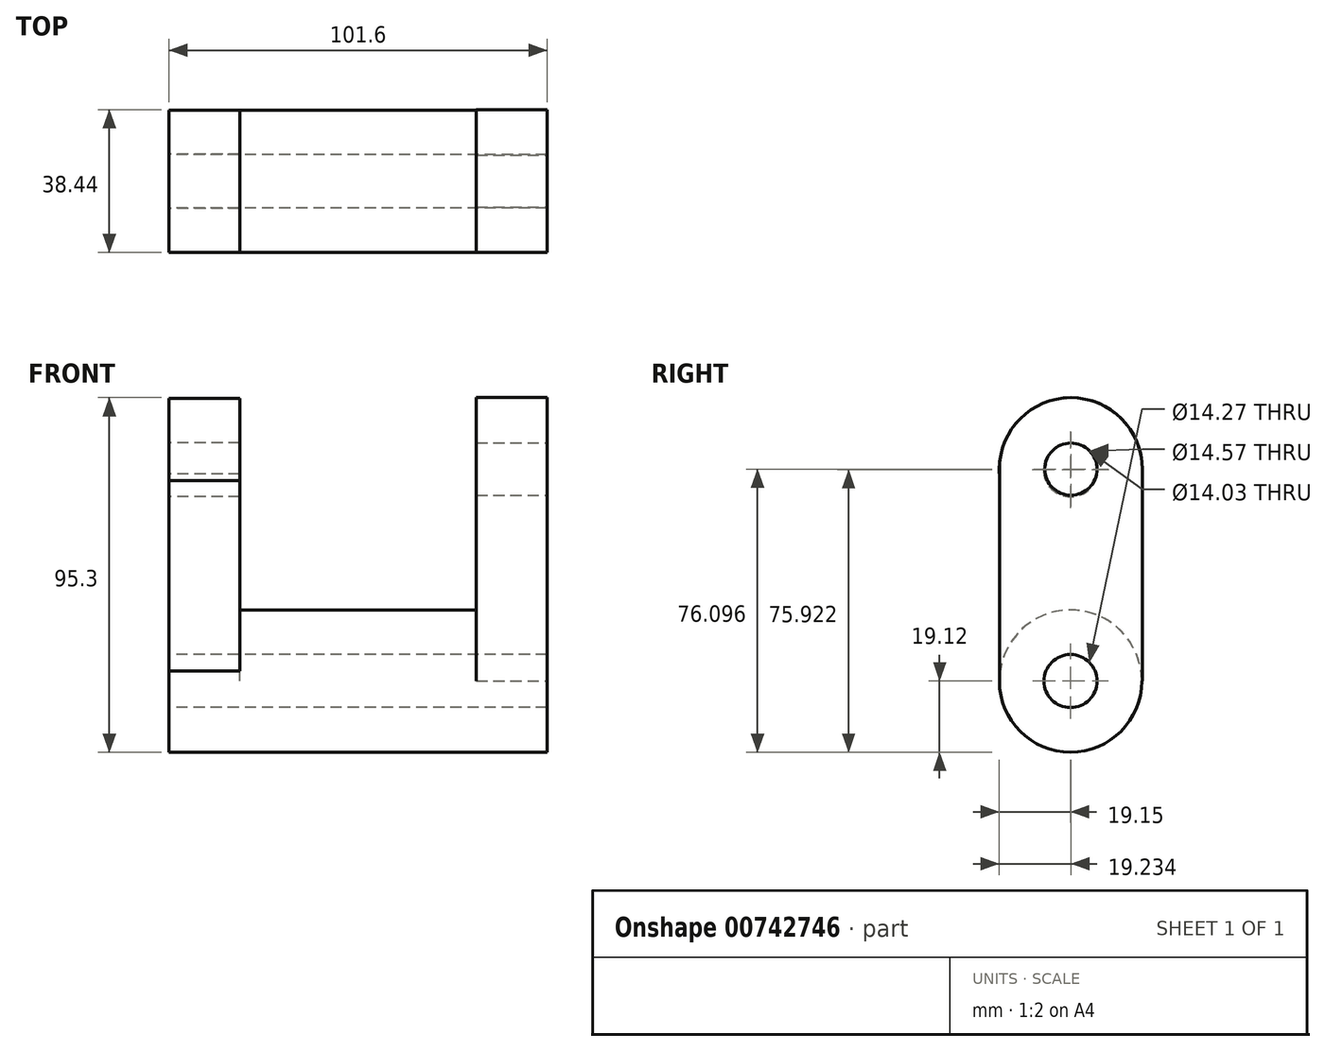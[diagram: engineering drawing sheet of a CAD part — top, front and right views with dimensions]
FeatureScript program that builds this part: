
annotation { "Feature Type Name" : "Feature", "Feature Type Description" : "" }
export const myFeature = defineFeature(function(context is Context, id is Id, definition is map)
    precondition{}
    {
        {
            var Q0;
            Q0=qCreatedBy(makeId("Right.planeOp"),FACE);
            var sketch = newSketch(context, id + "F0", { "sketchPlane" : qUnion([Q0])});
            skCircle(sketch, "E0", {"center": v(0, 0) * mm, "radius": 19.12 * mm});
            skCircle(sketch, "E1", {"center": v(0, 0) * mm, "radius": 7.13 * mm});
            skSolve(sketch);
        }
        {
            var Q0;
            Q0=makeQuery(id+"F0.imprint","IMPRINT",FACE,{"disambiguationData":[TD([[makeQuery(id+"F0.imprint","IMPRINT",EDGE,{"derivedFrom":sQuery(id+"F0.wireOp",EDGE,"E0")}),1.0]])]});
            extrude(context, id + "F1", {"entities" : qUnion([Q0]), "depth" : 50.8 * mm, "offsetDistance" : 25.4 * mm, "hasSecondDirection" : true, "secondDirectionOppositeDirection" : true, "secondDirectionDepth" : 50.8 * mm});
        }
        {
            var Q0;
            Q0=makeQuery(id+"F1.opExtrude","CAP_FACE",FACE,{"disambiguationData":[OSD([sQuery(id+"F0.wireOp",EDGE,"E0"),sQuery(id+"F0.wireOp",EDGE,"E1")])],"isStart":false});
            var sketch = newSketch(context, id + "F2", { "sketchPlane" : qUnion([Q0])});
            skLineSegment(sketch, "E2.bottom", {"start": v(-19.12, 0) * mm, "end": v(19.29, 0) * mm});
            skLineSegment(sketch, "E2.top", {"start": v(-19.12, 56.98) * mm, "end": v(19.29, 56.98) * mm});
            skLineSegment(sketch, "E2.left", {"start": v(-19.12, 0) * mm, "end": v(-19.12, 56.98) * mm});
            skLineSegment(sketch, "E2.right", {"start": v(19.29, 0) * mm, "end": v(19.29, 56.98) * mm});
            skCircle(sketch, "E3", {"center": v(0.08, 56.98) * mm, "radius": 19.2 * mm});
            skCircle(sketch, "E4", {"center": v(0.08, 56.98) * mm, "radius": 7.01 * mm});
            skSolve(sketch);
        }
        {
            var Q0;
            Q0=makeQuery(id+"F1.opExtrude","CAP_FACE",FACE,{"disambiguationData":[OSD([sQuery(id+"F0.wireOp",EDGE,"E0"),sQuery(id+"F0.wireOp",EDGE,"E1")])],"isStart":true});
            var sketch = newSketch(context, id + "F3", { "sketchPlane" : qUnion([Q0])});
            skLineSegment(sketch, "E5.bottom", {"start": v(-19.12, 0) * mm, "end": v(18.93, 0) * mm});
            skLineSegment(sketch, "E5.top", {"start": v(-19.12, 56.8) * mm, "end": v(18.93, 56.8) * mm});
            skLineSegment(sketch, "E5.left", {"start": v(-19.12, 0) * mm, "end": v(-19.12, 56.8) * mm});
            skLineSegment(sketch, "E5.right", {"start": v(18.93, 0) * mm, "end": v(18.93, 56.8) * mm});
            skCircle(sketch, "E6", {"center": v(0, 56.8) * mm, "radius": 19.15 * mm});
            skCircle(sketch, "E7", {"center": v(0, 56.8) * mm, "radius": 7.29 * mm});
            skSolve(sketch);
        }
        {
            var Q0;
            {var subQ3=sQuery(id+"F3.wireOp",EDGE,"E6");var subQ5=sQuery(id+"F3.wireOp",EDGE,"E5.right");var subQ6=makeQuery(id+"F3.imprint","INTERSECT",VERTEX,{"derivedFrom":[subQ5,subQ3]});Q0=makeQuery(id+"F3.imprint","IMPRINT",FACE,{"disambiguationData":[TD([[makeQuery(id+"F3.imprint","IMPRINT",EDGE,{"disambiguationData":[TD([[subQ6,1.0]])],"derivedFrom":subQ5}),1.0]])]});}
            var Q1;
            {var subQ0=sQuery(id+"F3.wireOp",EDGE,"E5.left");var subQ1=sQuery(id+"F3.wireOp",EDGE,"E5.top");var subQ2=makeQuery(id+"F3.imprint","INTERSECT",VERTEX,{"derivedFrom":[subQ1,subQ0]});Q1=makeQuery(id+"F3.imprint","IMPRINT",FACE,{"disambiguationData":[TD([[makeQuery(id+"F3.imprint","IMPRINT",EDGE,{"disambiguationData":[TD([[subQ2,-1.0]])],"derivedFrom":subQ1}),1.0]])]});}
            var Q2;
            {var subQ0=sQuery(id+"F3.wireOp",EDGE,"E5.left");var subQ1=sQuery(id+"F3.wireOp",EDGE,"E5.top");var subQ2=makeQuery(id+"F3.imprint","INTERSECT",VERTEX,{"derivedFrom":[subQ1,subQ0]});Q2=makeQuery(id+"F3.imprint","IMPRINT",FACE,{"disambiguationData":[TD([[makeQuery(id+"F3.imprint","IMPRINT",EDGE,{"disambiguationData":[TD([[subQ2,-1.0]])],"derivedFrom":subQ1}),-1.0]])]});}
            extrude(context, id + "F4", {"entities" : qUnion([Q0, Q1, Q2]), "operationType" : NewBodyOperationType.ADD, "oppositeDirection" : true, "depth" : 19.05 * mm, "offsetDistance" : 25.4 * mm});
        }
        {
            var Q0;
            {var subQ1=sQuery(id+"F2.wireOp",EDGE,"E2.left");Q0=makeQuery(id+"F2.imprint","IMPRINT",FACE,{"disambiguationData":[TD([[makeQuery(id+"F2.imprint","IMPRINT",EDGE,{"derivedFrom":subQ1}),-1.0]])]});}
            var Q1;
            {var subQ1=sQuery(id+"F2.wireOp",EDGE,"E2.top");var subQ3=sQuery(id+"F2.wireOp",EDGE,"E4");var subQ4=makeQuery(id+"F2.imprint","INTERSECT",VERTEX,{"disambiguationData":[OD(0.0)],"derivedFrom":[subQ1,subQ3]});Q1=makeQuery(id+"F2.imprint","IMPRINT",FACE,{"disambiguationData":[TD([[makeQuery(id+"F2.imprint","IMPRINT",EDGE,{"disambiguationData":[TD([[subQ4,1.0]])],"derivedFrom":subQ3}),-1.0]])]});}
            var Q2;
            {var subQ1=sQuery(id+"F2.wireOp",EDGE,"E2.top");var subQ3=sQuery(id+"F2.wireOp",EDGE,"E4");var subQ4=makeQuery(id+"F2.imprint","INTERSECT",VERTEX,{"disambiguationData":[OD(0.0)],"derivedFrom":[subQ1,subQ3]});Q2=makeQuery(id+"F2.imprint","IMPRINT",FACE,{"disambiguationData":[TD([[makeQuery(id+"F2.imprint","IMPRINT",EDGE,{"disambiguationData":[TD([[subQ4,-1.0]])],"derivedFrom":subQ3}),-1.0]])]});}
            extrude(context, id + "F5", {"entities" : qUnion([Q0, Q1, Q2]), "operationType" : NewBodyOperationType.ADD, "oppositeDirection" : true, "depth" : 19.05 * mm, "offsetDistance" : 25.4 * mm});
        }
    });
